# Revit family: Casement_30.5_C_Side_Hung_Standard
name_source: partatom
category: Windows
revit_build: Autodesk Revit 2014 (Build: 20130308_1515(x64)
units: mm (PartAtom-declared; Revit-internal decimal feet)

## types (12) — shared parameters
Aluminium Thickness = 1 mm  [stored 0.00328084 ft]
Bead SG Gap = 13 mm  [stored 0.0426509 ft]
Casement Dimension = 31 mm  [stored 0.101706 ft]
Custom Sash Left Width = 554 mm  [stored 1.81759 ft]
Custom Sash Right Width = 554 mm  [stored 1.81759 ft]
DG Extrusion Start = 5 mm  [stored 0.0164042 ft]
DG Gasket Finish = Double Glazing Gasket Material
DG Thickness = 3 mm  [stored 0.00984252 ft]
Default Sill Height = 800 mm  [stored 2.62467 ft]
Depth Bead = 17 mm
Depth Mullion = 32 mm
Description = Window 30.5mm, Type C side hung
Double Glazing = No
Frame Center Offset = 15 mm  [stored 0.0492126 ft]
Limit Fixed Pane Width Max = 1500 mm
Limit Fixed Pane Width Min = 200 mm  [stored 0.656168 ft]
Limit Sash Height Max = 1200 mm
Limit Sash Height Min = 300 mm  [stored 0.984252 ft]
Limit Sash Width Max = 600 mm  [stored 1.9685 ft]
Limit Sash Width Min = 300 mm  [stored 0.984252 ft]
Limit Window Height Max = 1246 mm  [stored 4.08793 ft]
Limit Window Height Min = 346 mm
Limit Window Width Max = 2700 mm
Limit Window Width Min = 1400 mm
Manufacturer = Crealco
Max System DG One Piece Thickness = 3 mm  [stored 0.00984252 ft]
Max System DG Unit Thickness = 18 mm  [stored 0.0590551 ft]
Model = Casement 30.5
Offset Bead Center Reversed = 15 mm  [stored 0.0492126 ft]
Offset Fixed Panel Left = 600 mm  [stored 1.9685 ft]
Offset Mullion Left Side = 570 mm  [stored 1.87008 ft]
Offset Mullion Right Side = 570 mm  [stored 1.87008 ft]
Offset Sash Side = 23 mm  [stored 0.0754593 ft]
Offset Sash Top = 23 mm  [stored 0.0754593 ft]
Offset Window Exterior = 15 mm  [stored 0.0492126 ft]
SG Gasket Thickness = 6 mm  [stored 0.019685 ft]
Sash Center Offset = 12 mm  [stored 0.0393701 ft]
Sash Overlap = 7 mm  [stored 0.0229659 ft]
Sash Spacing Inner = 8 mm  [stored 0.0262467 ft]
Side Hung Left = Yes
Side Hung Right = No
URL = http://www.crealco.co.za
Wall Closure = By host
Width Bead = 15 mm  [stored 0.0492126 ft]
Width Profile = 30 mm  [stored 0.0984252 ft]
Width Sash Left = 554 mm  [stored 1.81759 ft]
Width Sash Left Opening = 524 mm  [stored 1.71916 ft]
Width Sash Right = 554 mm  [stored 1.81759 ft]
Width Sash Right Opening = 524 mm  [stored 1.71916 ft]
zero-valued in all types: Window Exterior Offset

## per-type parameters (varying)
- 305-1809SS-1000Pa: Area Pane Left=0.35 m²; Area Pane Middle=0.48 m²; Area Pane Right=0.35 m²; Clearvue SHGC Value=0.608; Clearvue U Value=6.22; Corrected Mullion Size=0 mm  [stored 0 ft]; Custom Windload=1000 mm  [stored 3.28084 ft]; Custom Window Height=890 mm  [stored 2.91995 ft]; Custom Window Width=1790 mm; DG Thickness Calc=3 mm  [stored 0.00984252 ft]; Energy Advantage SHGC Value=0.544; Energy Advantage U Value=4.66; Height=890 mm  [stored 2.91995 ft]; Height Fixed Panel Center=830 mm  [stored 2.7231 ft]; Height Sash=814 mm  [stored 2.6706 ft]; Height Sash Opening=844 mm  [stored 2.76903 ft]; Intruderprufe LowE SHGC Value=0.571; Intruderprufe LowE U Value=4.55; Intruderprufe SHGC Value=0.579; Intruderprufe U Value=6.08; Length Mullion=890 mm  [stored 2.91995 ft]; Max Pane Area=0.48 m²; Mullion Depth Windload Based=32 mm; Sash Height=845 mm  [stored 2.77231 ft]; Standard Mullion Different=0 mm  [stored 0 ft]; Width=1790 mm; Width Fixed Panel Center=590 mm; Windload Design=1000 mm  [stored 3.28084 ft]
- 305-2409SS-1000Pa: Area Pane Left=0.35 m²; Area Pane Middle=0.97 m²; Area Pane Right=0.35 m²; Clearvue SHGC Value=0.645; Clearvue U Value=6.15; Corrected Mullion Size=0 mm  [stored 0 ft]; Custom Windload=1000 mm  [stored 3.28084 ft]; Custom Window Height=890 mm  [stored 2.91995 ft]; Custom Window Width=2390 mm; DG Thickness Calc=3 mm  [stored 0.00984252 ft]; Energy Advantage SHGC Value=0.577; Energy Advantage U Value=4.5; Height=890 mm  [stored 2.91995 ft]; Height Fixed Panel Center=830 mm  [stored 2.7231 ft]; Height Sash=814 mm  [stored 2.6706 ft]; Height Sash Opening=844 mm  [stored 2.76903 ft]; Intruderprufe LowE SHGC Value=0.542; Intruderprufe LowE U Value=4.4; Intruderprufe SHGC Value=0.614; Intruderprufe U Value=6.01; Length Mullion=890 mm  [stored 2.91995 ft]; Max Pane Area=0.97 m²; Mullion Depth Windload Based=32 mm; Sash Height=845 mm  [stored 2.77231 ft]; Standard Mullion Different=0 mm  [stored 0 ft]; Width=2390 mm; Width Fixed Panel Center=1190 mm  [stored 3.9042 ft]; Windload Design=1000 mm  [stored 3.28084 ft]
- 305-2409SS-1500Pa: Area Pane Left=0.35 m²; Area Pane Middle=0.97 m²; Area Pane Right=0.35 m²; Clearvue SHGC Value=0.646; Clearvue U Value=6.15; Corrected Mullion Size=0 mm  [stored 0 ft]; Custom Windload=1500 mm; Custom Window Height=890 mm  [stored 2.91995 ft]; Custom Window Width=2390 mm; DG Thickness Calc=3 mm  [stored 0.00984252 ft]; Energy Advantage SHGC Value=0.578; Energy Advantage U Value=4.6; Height=890 mm  [stored 2.91995 ft]; Height Fixed Panel Center=830 mm  [stored 2.7231 ft]; Height Sash=814 mm  [stored 2.6706 ft]; Height Sash Opening=844 mm  [stored 2.76903 ft]; Intruderprufe LowE SHGC Value=0.543; Intruderprufe LowE U Value=4.5; Intruderprufe SHGC Value=0.614; Intruderprufe U Value=6.01; Length Mullion=890 mm  [stored 2.91995 ft]; Max Pane Area=0.97 m²; Mullion Depth Windload Based=32 mm; Sash Height=845 mm  [stored 2.77231 ft]; Standard Mullion Different=0 mm  [stored 0 ft]; Width=2390 mm; Width Fixed Panel Center=1190 mm  [stored 3.9042 ft]; Windload Design=1500 mm
- 305-1812SS-1000Pa: Area Pane Left=0.49 m²; Area Pane Middle=0.65 m²; Area Pane Right=0.49 m²; Clearvue SHGC Value=0.632; Clearvue U Value=6.2; Corrected Mullion Size=32 mm; Custom Windload=1000 mm  [stored 3.28084 ft]; Custom Window Height=1190 mm  [stored 3.9042 ft]; Custom Window Width=1790 mm; DG Thickness Calc=3 mm  [stored 0.00984252 ft]; Energy Advantage SHGC Value=0.565; Energy Advantage U Value=4.57; Height=1190 mm  [stored 3.9042 ft]; Height Fixed Panel Center=1130 mm  [stored 3.70735 ft]; Height Sash=1114 mm  [stored 3.65486 ft]; Height Sash Opening=1144 mm; Intruderprufe LowE SHGC Value=0.531; Intruderprufe LowE U Value=4.47; Intruderprufe SHGC Value=0.602; Intruderprufe U Value=6.07; Length Mullion=1190 mm  [stored 3.9042 ft]; Max Pane Area=0.65 m²; Mullion Depth Windload Based=32 mm; Sash Height=1145 mm  [stored 3.75656 ft]; Standard Mullion Different=1 mm  [stored 0.00328084 ft]; Width=1790 mm; Width Fixed Panel Center=590 mm; Windload Design=1000 mm  [stored 3.28084 ft]
- 305-2412SS-1000Pa: Area Pane Left=0.49 m²; Area Pane Middle=1.32 m²; Area Pane Right=0.49 m²; Clearvue SHGC Value=0.67; Clearvue U Value=6.14; Corrected Mullion Size=0 mm  [stored 0 ft]; Custom Windload=1000 mm  [stored 3.28084 ft]; Custom Window Height=1190 mm  [stored 3.9042 ft]; Custom Window Width=2390 mm; DG Thickness Calc=4 mm  [stored 0.0131234 ft]; Energy Advantage SHGC Value=0.6; Energy Advantage U Value=4.51; Height=1190 mm  [stored 3.9042 ft]; Height Fixed Panel Center=1130 mm  [stored 3.70735 ft]; Height Sash=1114 mm  [stored 3.65486 ft]; Height Sash Opening=1144 mm; Intruderprufe LowE SHGC Value=0.562; Intruderprufe LowE U Value=4.42; Intruderprufe SHGC Value=0.637; Intruderprufe U Value=6; Length Mullion=1190 mm  [stored 3.9042 ft]; Max Pane Area=1.32 m²; Mullion Depth Windload Based=54 mm  [stored 0.177165 ft]; Sash Height=1145 mm  [stored 3.75656 ft]; Standard Mullion Different=0 mm  [stored 0 ft]; Width=2390 mm; Width Fixed Panel Center=1190 mm  [stored 3.9042 ft]; Windload Design=1000 mm  [stored 3.28084 ft]
- 305-1809SS-1500Pa: Area Pane Left=0.35 m²; Area Pane Middle=0.48 m²; Area Pane Right=0.35 m²; Clearvue SHGC Value=0.608; Clearvue U Value=6.22; Corrected Mullion Size=0 mm  [stored 0 ft]; Custom Windload=1500 mm; Custom Window Height=890 mm  [stored 2.91995 ft]; Custom Window Width=1790 mm; DG Thickness Calc=3 mm  [stored 0.00984252 ft]; Energy Advantage SHGC Value=0.544; Energy Advantage U Value=4.66; Height=890 mm  [stored 2.91995 ft]; Height Fixed Panel Center=830 mm  [stored 2.7231 ft]; Height Sash=814 mm  [stored 2.6706 ft]; Height Sash Opening=844 mm  [stored 2.76903 ft]; Intruderprufe LowE SHGC Value=0.571; Intruderprufe LowE U Value=4.55; Intruderprufe SHGC Value=0.579; Intruderprufe U Value=6.08; Length Mullion=890 mm  [stored 2.91995 ft]; Max Pane Area=0.48 m²; Mullion Depth Windload Based=32 mm; Sash Height=845 mm  [stored 2.77231 ft]; Standard Mullion Different=0 mm  [stored 0 ft]; Width=1790 mm; Width Fixed Panel Center=590 mm; Windload Design=1500 mm
- 305-1809SS-2000Pa: Area Pane Left=0.35 m²; Area Pane Middle=0.48 m²; Area Pane Right=0.35 m²; Clearvue SHGC Value=0.608; Clearvue U Value=6.22; Corrected Mullion Size=0 mm  [stored 0 ft]; Custom Windload=2000 mm; Custom Window Height=890 mm  [stored 2.91995 ft]; Custom Window Width=1790 mm; DG Thickness Calc=3 mm  [stored 0.00984252 ft]; Energy Advantage SHGC Value=0.544; Energy Advantage U Value=4.66; Height=890 mm  [stored 2.91995 ft]; Height Fixed Panel Center=830 mm  [stored 2.7231 ft]; Height Sash=814 mm  [stored 2.6706 ft]; Height Sash Opening=844 mm  [stored 2.76903 ft]; Intruderprufe LowE SHGC Value=0.571; Intruderprufe LowE U Value=4.55; Intruderprufe SHGC Value=0.579; Intruderprufe U Value=6.08; Length Mullion=890 mm  [stored 2.91995 ft]; Max Pane Area=0.48 m²; Mullion Depth Windload Based=32 mm; Sash Height=845 mm  [stored 2.77231 ft]; Standard Mullion Different=0 mm  [stored 0 ft]; Width=1790 mm; Width Fixed Panel Center=590 mm; Windload Design=2000 mm
- 305-1812SS-1500Pa: Area Pane Left=0.49 m²; Area Pane Middle=0.65 m²; Area Pane Right=0.49 m²; Clearvue SHGC Value=0.632; Clearvue U Value=6.2; Corrected Mullion Size=32 mm; Custom Windload=1500 mm; Custom Window Height=1190 mm  [stored 3.9042 ft]; Custom Window Width=1790 mm; DG Thickness Calc=3 mm  [stored 0.00984252 ft]; Energy Advantage SHGC Value=0.565; Energy Advantage U Value=4.57; Height=1190 mm  [stored 3.9042 ft]; Height Fixed Panel Center=1130 mm  [stored 3.70735 ft]; Height Sash=1114 mm  [stored 3.65486 ft]; Height Sash Opening=1144 mm; Intruderprufe LowE SHGC Value=0.531; Intruderprufe LowE U Value=4.47; Intruderprufe SHGC Value=0.602; Intruderprufe U Value=6.07; Length Mullion=1190 mm  [stored 3.9042 ft]; Max Pane Area=0.65 m²; Mullion Depth Windload Based=32 mm; Sash Height=1145 mm  [stored 3.75656 ft]; Standard Mullion Different=1 mm  [stored 0.00328084 ft]; Width=1790 mm; Width Fixed Panel Center=590 mm; Windload Design=1500 mm
- 305-1812SS-2000Pa: Area Pane Left=0.49 m²; Area Pane Middle=0.65 m²; Area Pane Right=0.49 m²; Clearvue SHGC Value=0.632; Clearvue U Value=6.2; Corrected Mullion Size=32 mm; Custom Windload=2000 mm; Custom Window Height=1190 mm  [stored 3.9042 ft]; Custom Window Width=1790 mm; DG Thickness Calc=3 mm  [stored 0.00984252 ft]; Energy Advantage SHGC Value=0.565; Energy Advantage U Value=4.57; Height=1190 mm  [stored 3.9042 ft]; Height Fixed Panel Center=1130 mm  [stored 3.70735 ft]; Height Sash=1114 mm  [stored 3.65486 ft]; Height Sash Opening=1144 mm; Intruderprufe LowE SHGC Value=0.531; Intruderprufe LowE U Value=4.47; Intruderprufe SHGC Value=0.602; Intruderprufe U Value=6.07; Length Mullion=1190 mm  [stored 3.9042 ft]; Max Pane Area=0.65 m²; Mullion Depth Windload Based=32 mm; Sash Height=1145 mm  [stored 3.75656 ft]; Standard Mullion Different=1 mm  [stored 0.00328084 ft]; Width=1790 mm; Width Fixed Panel Center=590 mm; Windload Design=2000 mm
- 305-2409SS-2000Pa: Area Pane Left=0.35 m²; Area Pane Middle=0.97 m²; Area Pane Right=0.35 m²; Clearvue SHGC Value=0.646; Clearvue U Value=6.15; Corrected Mullion Size=0 mm  [stored 0 ft]; Custom Windload=2000 mm; Custom Window Height=890 mm  [stored 2.91995 ft]; Custom Window Width=2390 mm; DG Thickness Calc=3 mm  [stored 0.00984252 ft]; Energy Advantage SHGC Value=0.578; Energy Advantage U Value=4.6; Height=890 mm  [stored 2.91995 ft]; Height Fixed Panel Center=830 mm  [stored 2.7231 ft]; Height Sash=814 mm  [stored 2.6706 ft]; Height Sash Opening=844 mm  [stored 2.76903 ft]; Intruderprufe LowE SHGC Value=0.543; Intruderprufe LowE U Value=4.5; Intruderprufe SHGC Value=0.614; Intruderprufe U Value=6.01; Length Mullion=890 mm  [stored 2.91995 ft]; Max Pane Area=0.97 m²; Mullion Depth Windload Based=54 mm  [stored 0.177165 ft]; Sash Height=845 mm  [stored 2.77231 ft]; Standard Mullion Different=0 mm  [stored 0 ft]; Width=2390 mm; Width Fixed Panel Center=1190 mm  [stored 3.9042 ft]; Windload Design=2000 mm
- 305-2412SS-1500Pa: Area Pane Left=0.49 m²; Area Pane Middle=1.32 m²; Area Pane Right=0.49 m²; Clearvue SHGC Value=0.67; Clearvue U Value=6.14; Corrected Mullion Size=0 mm  [stored 0 ft]; Custom Windload=1500 mm; Custom Window Height=1190 mm  [stored 3.9042 ft]; Custom Window Width=2390 mm; DG Thickness Calc=4 mm  [stored 0.0131234 ft]; Energy Advantage SHGC Value=0.6; Energy Advantage U Value=4.51; Height=1190 mm  [stored 3.9042 ft]; Height Fixed Panel Center=1130 mm  [stored 3.70735 ft]; Height Sash=1114 mm  [stored 3.65486 ft]; Height Sash Opening=1144 mm; Intruderprufe LowE SHGC Value=0.562; Intruderprufe LowE U Value=4.42; Intruderprufe SHGC Value=0.637; Intruderprufe U Value=6; Length Mullion=1190 mm  [stored 3.9042 ft]; Max Pane Area=1.32 m²; Mullion Depth Windload Based=54 mm  [stored 0.177165 ft]; Sash Height=1145 mm  [stored 3.75656 ft]; Standard Mullion Different=0 mm  [stored 0 ft]; Width=2390 mm; Width Fixed Panel Center=1190 mm  [stored 3.9042 ft]; Windload Design=1500 mm
- 305-2412SS-2000Pa: Area Pane Left=0.49 m²; Area Pane Middle=1.32 m²; Area Pane Right=0.49 m²; Clearvue SHGC Value=0.67; Clearvue U Value=6.14; Corrected Mullion Size=0 mm  [stored 0 ft]; Custom Windload=2000 mm; Custom Window Height=1190 mm  [stored 3.9042 ft]; Custom Window Width=2390 mm; DG Thickness Calc=4 mm  [stored 0.0131234 ft]; Energy Advantage SHGC Value=0.6; Energy Advantage U Value=4.51; Height=1190 mm  [stored 3.9042 ft]; Height Fixed Panel Center=1130 mm  [stored 3.70735 ft]; Height Sash=1114 mm  [stored 3.65486 ft]; Height Sash Opening=1144 mm; Intruderprufe LowE SHGC Value=0.562; Intruderprufe LowE U Value=4.42; Intruderprufe SHGC Value=0.637; Intruderprufe U Value=6; Length Mullion=1190 mm  [stored 3.9042 ft]; Max Pane Area=1.32 m²; Mullion Depth Windload Based=54 mm  [stored 0.177165 ft]; Sash Height=1145 mm  [stored 3.75656 ft]; Standard Mullion Different=0 mm  [stored 0 ft]; Width=2390 mm; Width Fixed Panel Center=1190 mm  [stored 3.9042 ft]; Windload Design=2000 mm

note: [stored X ft] marks values corroborated as IEEE doubles in the binary element streams (Revit-internal decimal feet)

## geometry (parser evidence)
native form markers: Extrusion x1, Sweep x29
no freeform markers — native parametric forms only
